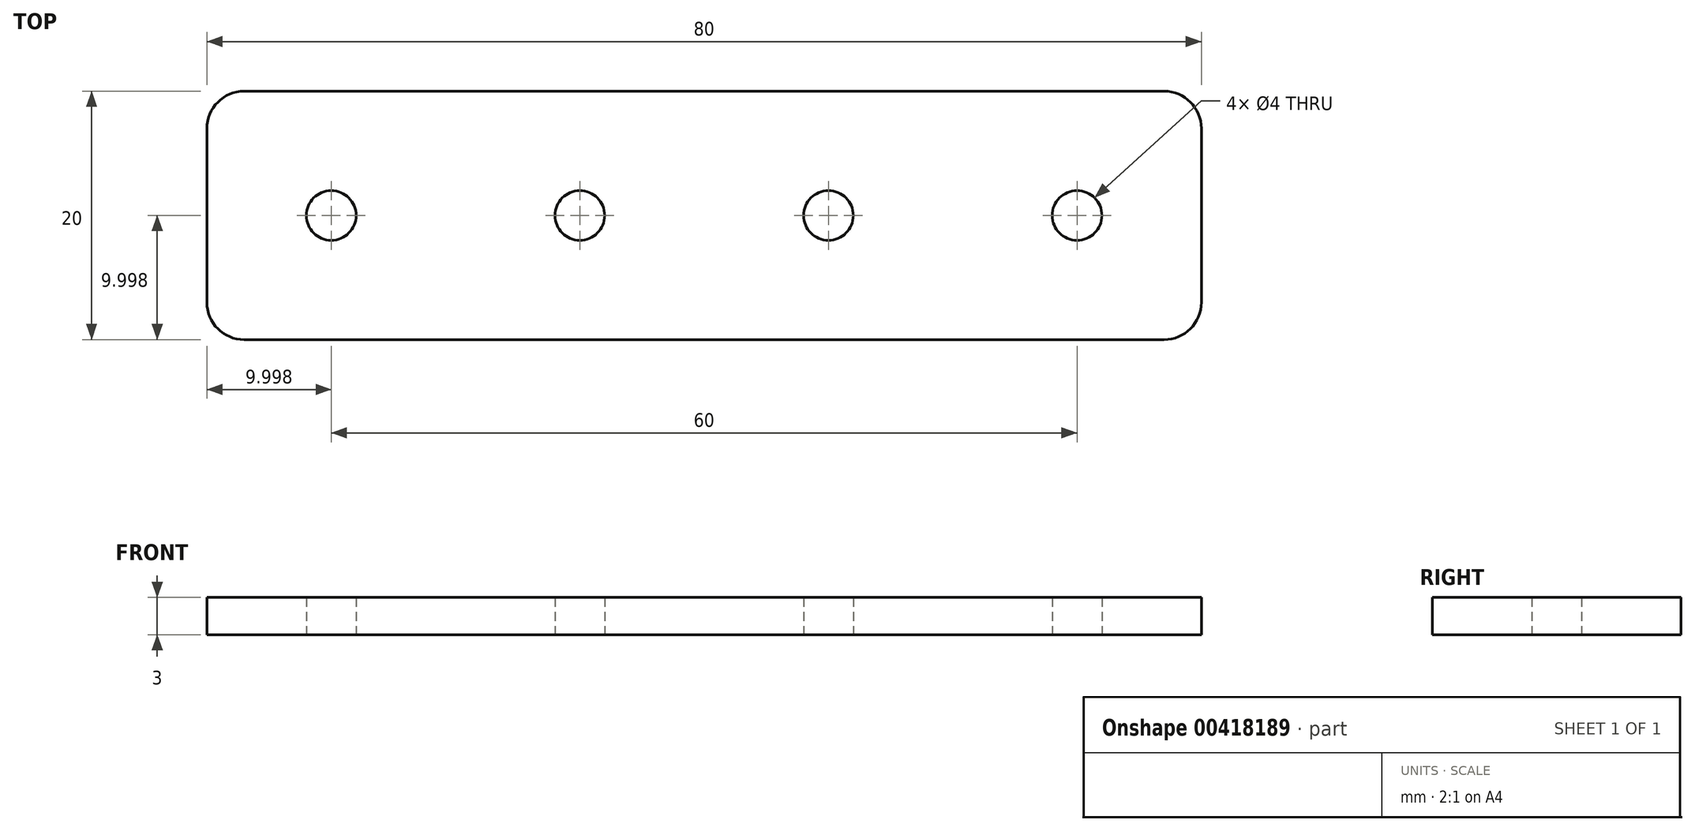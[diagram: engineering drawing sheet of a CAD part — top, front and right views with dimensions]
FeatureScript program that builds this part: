
annotation { "Feature Type Name" : "Feature", "Feature Type Description" : "" }
export const myFeature = defineFeature(function(context is Context, id is Id, definition is map)
    precondition{}
    {
        {
            var Q0;
            Q0=qCreatedBy(makeId("Top.planeOp"),FACE);
            var sketch = newSketch(context, id + "F0", { "sketchPlane" : qUnion([Q0])});
            skLineSegment(sketch, "E0.bottom", {"start": v(-82.48, 43.76) * mm, "end": v(-8.48, 43.76) * mm});
            skLineSegment(sketch, "E0.top", {"start": v(-82.48, 23.76) * mm, "end": v(-8.48, 23.76) * mm});
            skLineSegment(sketch, "E0.left", {"start": v(-85.48, 40.76) * mm, "end": v(-85.48, 26.76) * mm});
            skLineSegment(sketch, "E0.right", {"start": v(-5.48, 40.76) * mm, "end": v(-5.48, 26.76) * mm});
            skCircle(sketch, "E1", {"center": v(-75.48, 33.76) * mm, "radius": 2 * mm});
            skCircle(sketch, "E2.1.0.0", {"center": v(-55.48, 33.76) * mm, "radius": 2 * mm});
            skCircle(sketch, "E2.2.0.0", {"center": v(-35.48, 33.76) * mm, "radius": 2 * mm});
            skCircle(sketch, "E2.3.0.0", {"center": v(-15.48, 33.76) * mm, "radius": 2 * mm});
            skLineSegment(sketch, "E2.direction1", {"start": v(-75.48, 33.76) * mm, "end": v(-55.48, 33.76) * mm, "construction": true});
            skPoint(sketch, "E3.visualSharp", {"position": v(-5.48, 43.76) * mm});
            skArc(sketch, "E3.filletArc", {"start": v(-5.48, 40.76) * mm, "mid": v(-6.36, 42.88) * mm, "end": v(-8.48, 43.76) * mm});
            skPoint(sketch, "E4.visualSharp", {"position": v(-5.48, 23.76) * mm});
            skArc(sketch, "E4.filletArc", {"start": v(-8.48, 23.76) * mm, "mid": v(-6.36, 24.64) * mm, "end": v(-5.48, 26.76) * mm});
            skPoint(sketch, "E5.visualSharp", {"position": v(-85.48, 23.76) * mm});
            skArc(sketch, "E5.filletArc", {"start": v(-85.48, 26.76) * mm, "mid": v(-84.6, 24.64) * mm, "end": v(-82.48, 23.76) * mm});
            skPoint(sketch, "E6.visualSharp", {"position": v(-85.48, 43.76) * mm});
            skArc(sketch, "E6.filletArc", {"start": v(-82.48, 43.76) * mm, "mid": v(-84.6, 42.88) * mm, "end": v(-85.48, 40.76) * mm});
            skSolve(sketch);
        }
        {
            var Q0;
            Q0 = qSketchRegion(id + "F0", true);
            extrude(context, id + "F1", {"entities" : qUnion([Q0]), "depth" : 3 * mm});
        }
    });
